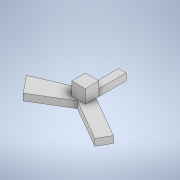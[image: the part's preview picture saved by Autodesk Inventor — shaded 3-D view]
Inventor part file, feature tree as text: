
AUTODESK INVENTOR PART (.ipt)
format: ipt  version: 2021.1 (Build 251245010, 245A)  size: 159,744 bytes
history: native  units: in
note: dims shown in document units (in); Inventor stores cm internally (conversion verified against a paired STEP export)
features: extrude x8, sketch x8, plane x2
ambient origin geometry x8: Origin, YZ Plane, XZ Plane, XY Plane, X Axis, Y Axis, Z Axis, Center Point
bodies: Solid1 (feature_tree)
feature tree (18):
  extrude  "Extrusion1"  Depth=1.0in
  extrude  "Extrusion8"  Depth=1.0in
  extrude  "Extrusion2"  Depth=1.0in
  extrude  "Extrusion3"  Depth=3.0in TaperAngle=0.0deg
  extrude  "Extrusion4"  Depth=0.5in TaperAngle=0.0deg
  extrude  "Extrusion5"  Depth=5.0in TaperAngle=0.0deg
  plane  "Work Plane2"
  extrude  "Extrusion6"  Depth=5.0in TaperAngle=0.0deg
  plane  "Work Plane4"
  extrude  "Extrusion7"  TaperAngle=0.0deg  [1 undecoded]
  sketch  "Sketch2"  dims[d0=1.0in d1=1.0in]
  sketch  "Sketch3"  dims[d2=1.0in d3=0.0in d4=1.0in]
  sketch  "Sketch4"  dims[d5=3.0in d6=0.0in d7=1.0in]
  sketch  "Sketch5"  dims[d8=3.0in d9=0.0in d10=3.0in d11=0.0in]
  sketch  "Sketch6"  dims[d12=0.5in d13=5.0in d14=0.0in]
  sketch  "Sketch7"  dims[d16=60.0deg d17=5.0in d18=0.0in]
  sketch  "Sketch8"  dims[d20=120.0deg d21=5.0in d22=0.0in]
  sketch  "Sketch9"  dims[d23=3.0in d24=0.0in d25=120.0deg d26=120.0deg d27=1.0in d28=0.5in d29=0.0in]
note: 1 required parameter value undecoded (feature->parameter linkage not recoverable at this tier; creation-order binding heuristic only, values carry confidence <= 0.55)
